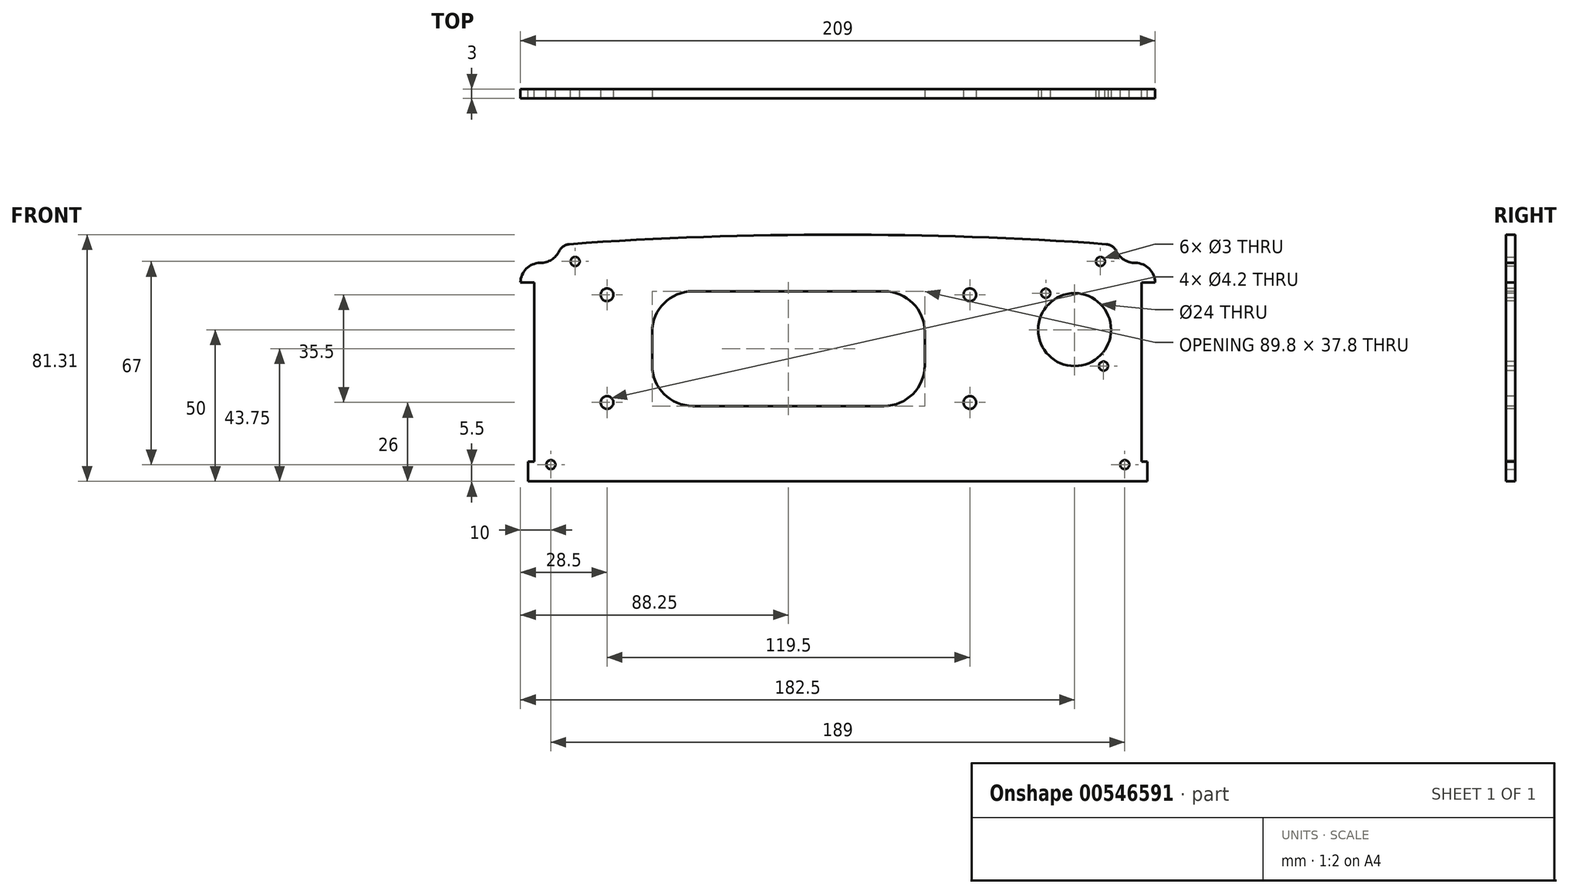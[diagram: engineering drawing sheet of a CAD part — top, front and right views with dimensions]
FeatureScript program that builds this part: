
annotation { "Feature Type Name" : "Feature", "Feature Type Description" : "" }
export const myFeature = defineFeature(function(context is Context, id is Id, definition is map)
    precondition{}
    {
        {
            var Q0;
            Q0=qCreatedBy(makeId("Front.planeOp"),FACE);
            var sketch = newSketch(context, id + "F0", { "sketchPlane" : qUnion([Q0])});
            skLineSegment(sketch, "E0.bottom", {"start": v(-102, -23) * mm, "end": v(0, -23) * mm});
            skLineSegment(sketch, "E0.top", {"start": v(-102, 42.5) * mm, "end": v(-100, 42.5) * mm});
            skLineSegment(sketch, "E0.left", {"start": v(-102, -23) * mm, "end": v(-102, -16.5) * mm});
            skLineSegment(sketch, "E1.left", {"start": v(-100, 42.5) * mm, "end": v(-100, -16.5) * mm});
            skLineSegment(sketch, "E2", {"start": v(-100, -16.5) * mm, "end": v(-102, -16.5) * mm});
            skLineSegment(sketch, "E3", {"start": v(0, -23) * mm, "end": v(0, 61.24) * mm, "construction": true});
            skPoint(sketch, "E3.endSnap0", {"position": v(0, 42.5) * mm});
            skLineSegment(sketch, "E4", {"start": v(-100, 42.5) * mm, "end": v(-104.5, 42.5) * mm});
            skArc(sketch, "E5", {"start": v(-98, 49) * mm, "mid": v(-102.6, 47.1) * mm, "end": v(-104.5, 42.5) * mm});
            skArc(sketch, "E6", {"start": v(-98, 49) * mm, "mid": v(-94.28, 50.07) * mm, "end": v(-91.7, 52.95) * mm});
            skArc(sketch, "E7", {"start": v(-88.4, 55.2) * mm, "mid": v(-90.35, 54.51) * mm, "end": v(-91.7, 52.95) * mm});
            skArc(sketch, "E8", {"start": v(0, 58.3) * mm, "mid": v(-44.23, 57.6) * mm, "end": v(-88.4, 55.2) * mm});
            skPoint(sketch, "E9.orphan", {"position": v(102, -23) * mm});
            skArc(sketch, "E10.MirrorCS", {"start": v(0, 58.3) * mm, "mid": v(44.23, 57.6) * mm, "end": v(88.4, 55.2) * mm});
            skArc(sketch, "E11.MirrorCS", {"start": v(88.4, 55.2) * mm, "mid": v(90.35, 54.51) * mm, "end": v(91.7, 52.95) * mm});
            skArc(sketch, "E12.MirrorCS", {"start": v(98, 49) * mm, "mid": v(94.28, 50.07) * mm, "end": v(91.7, 52.95) * mm});
            skArc(sketch, "E13.MirrorCS", {"start": v(98, 49) * mm, "mid": v(102.6, 47.1) * mm, "end": v(104.5, 42.5) * mm});
            skLineSegment(sketch, "E14.MirrorCS", {"start": v(100, 42.5) * mm, "end": v(104.5, 42.5) * mm});
            skLineSegment(sketch, "E15.MirrorCS", {"start": v(100, 42.5) * mm, "end": v(100, -16.5) * mm});
            skLineSegment(sketch, "E16.MirrorCS", {"start": v(100, -16.5) * mm, "end": v(102, -16.5) * mm});
            skLineSegment(sketch, "E17.MirrorCS", {"start": v(102, -23) * mm, "end": v(102, -16.5) * mm});
            skLineSegment(sketch, "E18.MirrorCS", {"start": v(102, -23) * mm, "end": v(0, -23) * mm});
            skLineSegment(sketch, "E19.trimOffspring", {"start": v(100, 42.5) * mm, "end": v(100, 42.5) * mm});
            skPoint(sketch, "E20.trimOffspring.end.orphan", {"position": v(100, 42.5) * mm});
            skCircle(sketch, "E21", {"center": v(-94.5, -17.5) * mm, "radius": 1.5 * mm});
            skCircle(sketch, "E22", {"center": v(-86.5, 49.5) * mm, "radius": 1.5 * mm});
            skCircle(sketch, "E23.MirrorC", {"center": v(94.5, -17.5) * mm, "radius": 1.5 * mm});
            skCircle(sketch, "E24", {"center": v(86.5, 49.5) * mm, "radius": 1.5 * mm});
            skSolve(sketch);
        }
        {
            var Q0;
            Q0=makeQuery(id+"F0.imprint","IMPRINT",FACE,{"disambiguationData":[TD([[makeQuery(id+"F0.imprint","IMPRINT",EDGE,{"derivedFrom":sQuery(id+"F0.wireOp",EDGE,"E0.bottom")}),1.0]])]});
            extrude(context, id + "F1", {"entities" : qUnion([Q0]), "depth" : 3 * mm, "offsetDistance" : 25 * mm});
        }
        {
            var Q0;
            Q0=makeQuery(id+"F1.opExtrude","CAP_FACE",FACE,{"disambiguationData":[OSD([sQuery(id+"F0.wireOp",EDGE,"E0.bottom"),sQuery(id+"F0.wireOp",EDGE,"E0.left"),sQuery(id+"F0.wireOp",EDGE,"E1.left"),sQuery(id+"F0.wireOp",EDGE,"E2"),sQuery(id+"F0.wireOp",EDGE,"E4"),sQuery(id+"F0.wireOp",EDGE,"E5"),sQuery(id+"F0.wireOp",EDGE,"E6"),sQuery(id+"F0.wireOp",EDGE,"E7"),sQuery(id+"F0.wireOp",EDGE,"E8"),sQuery(id+"F0.wireOp",EDGE,"E10.MirrorCS"),sQuery(id+"F0.wireOp",EDGE,"E11.MirrorCS"),sQuery(id+"F0.wireOp",EDGE,"E12.MirrorCS"),sQuery(id+"F0.wireOp",EDGE,"E13.MirrorCS"),sQuery(id+"F0.wireOp",EDGE,"E14.MirrorCS"),sQuery(id+"F0.wireOp",EDGE,"E15.MirrorCS"),sQuery(id+"F0.wireOp",EDGE,"E16.MirrorCS"),sQuery(id+"F0.wireOp",EDGE,"E17.MirrorCS"),sQuery(id+"F0.wireOp",EDGE,"E18.MirrorCS"),sQuery(id+"F0.wireOp",EDGE,"E19.trimOffspring"),sQuery(id+"F0.wireOp",EDGE,"E21"),sQuery(id+"F0.wireOp",EDGE,"E22"),sQuery(id+"F0.wireOp",EDGE,"cb757283-0561-4789-a358-3e201053efa00.MirrorC"),sQuery(id+"F0.wireOp",EDGE,"E23.MirrorC")])],"isStart":false});
            var sketch = newSketch(context, id + "F2", { "sketchPlane" : qUnion([Q0])});
            skCircle(sketch, "E25", {"center": v(78, 27) * mm, "radius": 12 * mm});
            skCircle(sketch, "E26", {"center": v(87.5, 15) * mm, "radius": 1.5 * mm});
            skCircle(sketch, "E27", {"center": v(68.5, 39) * mm, "radius": 1.5 * mm});
            skSolve(sketch);
        }
        {
            var Q0;
            Q0 = qSketchRegion(id + "F2", true);
            extrude(context, id + "F3", {"entities" : qUnion([Q0]), "operationType" : NewBodyOperationType.REMOVE, "oppositeDirection" : true, "depth" : 25 * mm, "offsetDistance" : 25 * mm});
        }
        {
            var Q0;
            Q0=makeQuery(id+"F1.opExtrude","CAP_FACE",FACE,{"disambiguationData":[OSD([sQuery(id+"F0.wireOp",EDGE,"E0.bottom"),sQuery(id+"F0.wireOp",EDGE,"E0.left"),sQuery(id+"F0.wireOp",EDGE,"E1.left"),sQuery(id+"F0.wireOp",EDGE,"E2"),sQuery(id+"F0.wireOp",EDGE,"E4"),sQuery(id+"F0.wireOp",EDGE,"E5"),sQuery(id+"F0.wireOp",EDGE,"E6"),sQuery(id+"F0.wireOp",EDGE,"E7"),sQuery(id+"F0.wireOp",EDGE,"E8"),sQuery(id+"F0.wireOp",EDGE,"E10.MirrorCS"),sQuery(id+"F0.wireOp",EDGE,"E11.MirrorCS"),sQuery(id+"F0.wireOp",EDGE,"E12.MirrorCS"),sQuery(id+"F0.wireOp",EDGE,"E13.MirrorCS"),sQuery(id+"F0.wireOp",EDGE,"E14.MirrorCS"),sQuery(id+"F0.wireOp",EDGE,"E15.MirrorCS"),sQuery(id+"F0.wireOp",EDGE,"E16.MirrorCS"),sQuery(id+"F0.wireOp",EDGE,"E17.MirrorCS"),sQuery(id+"F0.wireOp",EDGE,"E18.MirrorCS"),sQuery(id+"F0.wireOp",EDGE,"E19.trimOffspring"),sQuery(id+"F0.wireOp",EDGE,"E21"),sQuery(id+"F0.wireOp",EDGE,"E22"),sQuery(id+"F0.wireOp",EDGE,"cb757283-0561-4789-a358-3e201053efa00.MirrorC"),sQuery(id+"F0.wireOp",EDGE,"E23.MirrorC")])],"isStart":false});
            var sketch = newSketch(context, id + "F4", { "sketchPlane" : qUnion([Q0])});
            skLineSegment(sketch, "E28.bottom", {"start": v(-47.75, 39.65) * mm, "end": v(15.25, 39.65) * mm});
            skLineSegment(sketch, "E28.top", {"start": v(-47.75, 1.85) * mm, "end": v(15.25, 1.85) * mm});
            skLineSegment(sketch, "E28.left", {"start": v(-61.15, 26.25) * mm, "end": v(-61.15, 15.25) * mm});
            skLineSegment(sketch, "E28.right", {"start": v(28.65, 26.25) * mm, "end": v(28.65, 15.25) * mm});
            skPoint(sketch, "E29.visualSharp", {"position": v(-61.15, 39.65) * mm});
            skArc(sketch, "E29.filletArc", {"start": v(-47.75, 39.65) * mm, "mid": v(-57.23, 35.73) * mm, "end": v(-61.15, 26.25) * mm});
            skPoint(sketch, "E30.visualSharp", {"position": v(28.65, 39.65) * mm});
            skArc(sketch, "E30.filletArc", {"start": v(28.65, 26.25) * mm, "mid": v(24.73, 35.73) * mm, "end": v(15.25, 39.65) * mm});
            skPoint(sketch, "E31.visualSharp", {"position": v(28.65, 1.85) * mm});
            skArc(sketch, "E31.filletArc", {"start": v(15.25, 1.85) * mm, "mid": v(24.73, 5.77) * mm, "end": v(28.65, 15.25) * mm});
            skPoint(sketch, "E32.visualSharp", {"position": v(-61.15, 1.85) * mm});
            skArc(sketch, "E32.filletArc", {"start": v(-61.15, 15.25) * mm, "mid": v(-57.23, 5.77) * mm, "end": v(-47.75, 1.85) * mm});
            skCircle(sketch, "E33", {"center": v(-76, 38.5) * mm, "radius": 2.1 * mm});
            skCircle(sketch, "E34", {"center": v(-76, 3) * mm, "radius": 2.1 * mm});
            skCircle(sketch, "E35", {"center": v(43.5, 3) * mm, "radius": 2.1 * mm});
            skCircle(sketch, "E36", {"center": v(43.5, 38.5) * mm, "radius": 2.1 * mm});
            skLineSegment(sketch, "E37", {"start": v(-61.15, 20.75) * mm, "end": v(28.65, 20.75) * mm, "construction": true});
            skLineSegment(sketch, "E38", {"start": v(-16.25, 39.65) * mm, "end": v(-16.25, 1.85) * mm, "construction": true});
            skSolve(sketch);
        }
        {
            var Q0;
            Q0 = qSketchRegion(id + "F4", true);
            extrude(context, id + "F5", {"entities" : qUnion([Q0]), "operationType" : NewBodyOperationType.REMOVE, "oppositeDirection" : true, "depth" : 25 * mm, "offsetDistance" : 25 * mm});
        }
    });
